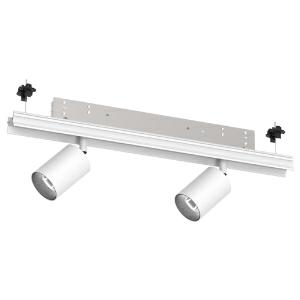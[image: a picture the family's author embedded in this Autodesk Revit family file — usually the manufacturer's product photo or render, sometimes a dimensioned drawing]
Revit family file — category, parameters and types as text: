
# Revit family: centriq_double_7-02804-00
name_source: partatom
category: Lighting Fixtures
units: mm (PartAtom-declared; Revit-internal decimal feet)

## family parameters
Cut with Voids When Loaded = No
Host = Face
Light Source = No
Part Type = Normal
Room Calculation Point = No
Round Connector Dimension = Use Diameter
Shared = No

## types (1)
- 7-02804-00-H27-K15 (1 x LED, 1140.96 lm, 12 W, 2700K)
    Apparent Load = 24 VA
    CIE Flux Codes = 98 100 100 100 68
    Color Rendering = 1A/90…99
    Color Temperature = 2700K
    Default Elevation = 1800 mm
    Description = CENTRIQ DOUBLE
    Height = 80 mm  [stored 0.262467 ft]
    Lamp = 1 x LED
    Lamp Light Flux = 1140.96 lm
    Lamp Power = 12 W
    Lamp count = 1
    Length = 56 mm
    Luminous efficacy = 64 lm/W
    Manufacturer = Prolicht
    ModVariant = No
    Model = 7-02804-00
    Mounting Place = Ceiling
    Mounting Type = Pendant
    Number of Poles = 1
    OnlyDefault = Yes
    Power Factor = 1
    Product Name = CENTRIQ DOUBLE
    Product group = Suspended spotlights
    ProductGroupID = 942
    Protection Class = Protection class
    Protection Degree = Degree of protection
    RLX_Detail_Level = 1
    RlxData = <blob elided: 131293 chars, md5=09e430a3>
    Socket = socket
    Standby Power = 0 W
    System Light Flux = 1545 lm
    System Power = 24 W
    Type Comments = LED COLOUR DIR 2700 K (27),REFLECTOR 15° (15)
    Type Image = 7-02804-00.jpg
    URL = http://relux.com
    VarID = 7-02804-00-h27-k15
    Voltage = 0 V
    Weight = 0.00 kg
    Width = 0 mm  [stored 0 ft]

note: [stored X ft] marks values corroborated as IEEE doubles in the binary element streams (Revit-internal decimal feet)

## geometry (parser evidence)
native form markers: Blend x4, Sweep x18
no freeform markers — native parametric forms only
